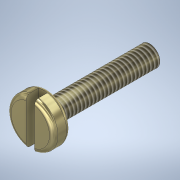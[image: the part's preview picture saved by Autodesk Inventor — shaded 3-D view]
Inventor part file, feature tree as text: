
AUTODESK INVENTOR PART (.ipt)
format: ipt  version: 2020 (Build 240168000, 168)  size: 166,400 bytes
history: native  units: mm
features: extrude x3, sketch x3, thread x1, fillet x1
ambient origin geometry x8: Origin, YZ Plane, XZ Plane, XY Plane, X Axis, Y Axis, Z Axis, Center Point
bodies: Solid1 (feature_tree)
feature tree (8):
  extrude  "Extrusion1"  Depth=2.0mm TaperAngle=0.0deg
  extrude  "Extrusion2"  Depth=5.5mm
  extrude  "Extrusion3"  Depth=0.5mm
  thread  "Thread2"  [1 undecoded]
  fillet  "Fillet1"  Radius=8.0mm
  sketch  "Sketch1"  dims[d0=5.5mm d1=2.0mm d2=0.0mm]
  sketch  "Sketch2"  dims[d3=1.0mm d4=5.5mm]
  sketch  "Sketch3"  dims[d5=1.5mm d6=0.0mm d7=2.4mm d8=12.0mm d9=0.0mm d12=8.0mm d13=0.0mm d14=0.5mm]
note: 1 required parameter value undecoded (feature->parameter linkage not recoverable at this tier; creation-order binding heuristic only, values carry confidence <= 0.55)
